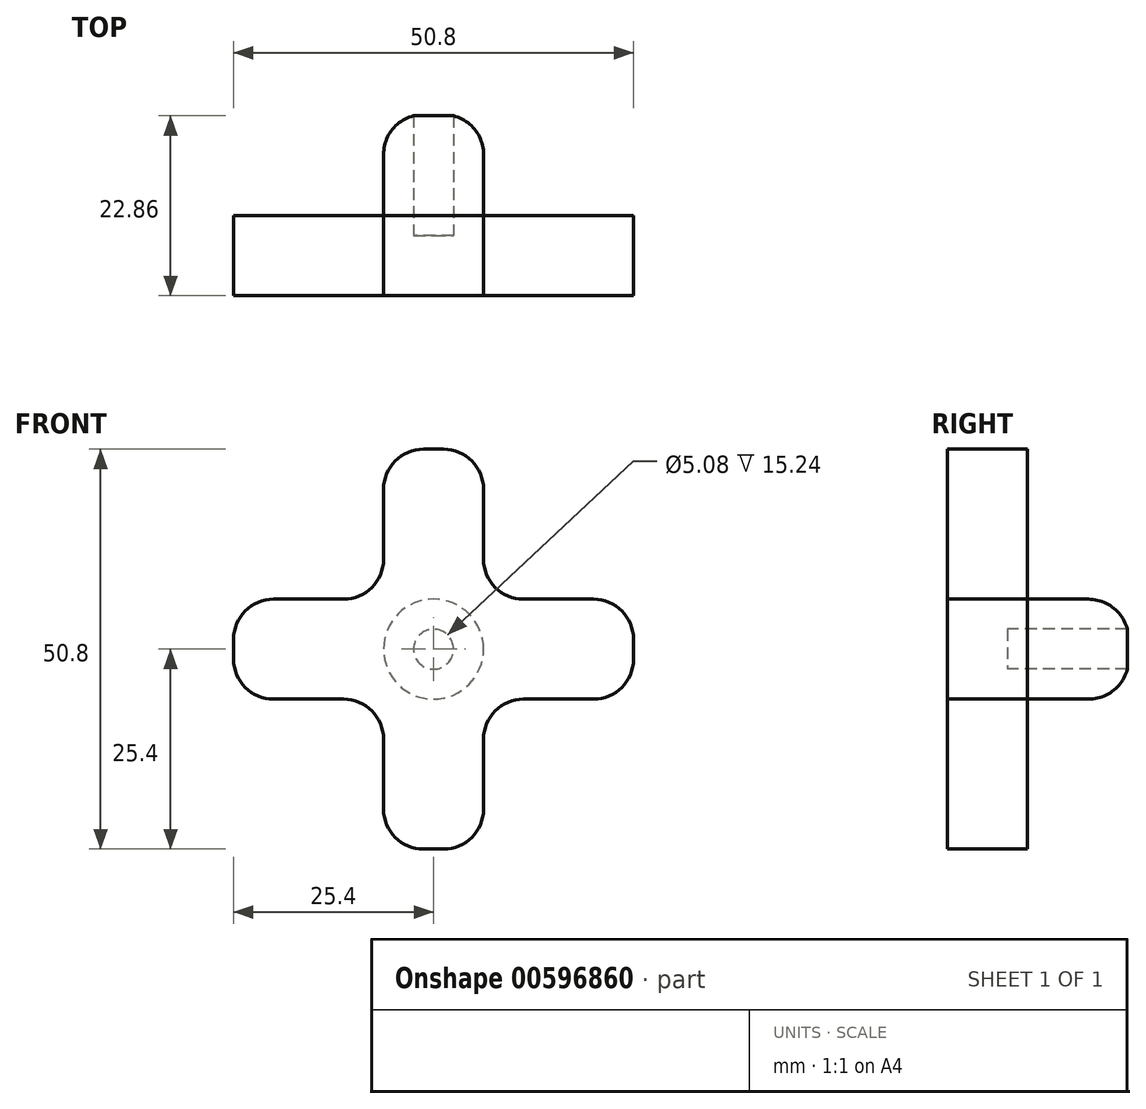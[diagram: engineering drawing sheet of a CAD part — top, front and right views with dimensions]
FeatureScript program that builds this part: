
annotation { "Feature Type Name" : "Feature", "Feature Type Description" : "" }
export const myFeature = defineFeature(function(context is Context, id is Id, definition is map)
    precondition{}
    {
        {
            var Q0;
            Q0=qCreatedBy(makeId("Front.planeOp"),FACE);
            var sketch = newSketch(context, id + "F0", { "sketchPlane" : qUnion([Q0])});
            skLineSegment(sketch, "E0.bottom", {"start": v(0, 0) * mm, "end": v(50.8, 0) * mm});
            skLineSegment(sketch, "E0.top", {"start": v(0, -12.7) * mm, "end": v(50.8, -12.7) * mm});
            skLineSegment(sketch, "E0.left", {"start": v(0, 0) * mm, "end": v(0, -12.7) * mm});
            skLineSegment(sketch, "E0.right", {"start": v(50.8, 0) * mm, "end": v(50.8, -12.7) * mm});
            skLineSegment(sketch, "E1.bottom", {"start": v(19.05, 19.05) * mm, "end": v(31.75, 19.05) * mm});
            skLineSegment(sketch, "E1.top", {"start": v(19.05, -31.75) * mm, "end": v(31.75, -31.75) * mm});
            skLineSegment(sketch, "E1.left", {"start": v(19.05, 19.05) * mm, "end": v(19.05, -31.75) * mm});
            skLineSegment(sketch, "E1.right", {"start": v(31.75, 19.05) * mm, "end": v(31.75, -31.75) * mm});
            skPoint(sketch, "E1.middle", {"position": v(25.4, -6.35) * mm});
            skPoint(sketch, "E1.middle.positionSnap0", {"position": v(0, -6.35) * mm});
            skPoint(sketch, "E1.middle.positionSnap1", {"position": v(25.4, -12.7) * mm});
            skPoint(sketch, "E1.centerSnap0", {"position": v(0, -6.35) * mm});
            skPoint(sketch, "E1.centerSnap1", {"position": v(25.4, -12.7) * mm});
            skSolve(sketch);
        }
        {
            var Q0;
            Q0 = qSketchRegion(id + "F0", true);
            extrude(context, id + "F1", {"entities" : qUnion([Q0]), "depth" : 10.16 * mm, "offsetDistance" : 25.4 * mm});
        }
        {
            var Q0;
            Q0=makeQuery(id+"F1.opExtrude","SWEPT_EDGE",EDGE,{"disambiguationData":[OSD([sQuery(id+"F0.wireOp",EDGE,"E0.top"),sQuery(id+"F0.wireOp",EDGE,"E1.left")])]});
            var Q1;
            Q1=makeQuery(id+"F1.opExtrude","SWEPT_EDGE",EDGE,{"disambiguationData":[OSD([sQuery(id+"F0.wireOp",EDGE,"E0.bottom"),sQuery(id+"F0.wireOp",EDGE,"E1.left")])]});
            var Q2;
            Q2=makeQuery(id+"F1.opExtrude","SWEPT_EDGE",EDGE,{"disambiguationData":[OSD([sQuery(id+"F0.wireOp",EDGE,"E0.bottom"),sQuery(id+"F0.wireOp",EDGE,"E1.right")])]});
            var Q3;
            Q3=makeQuery(id+"F1.opExtrude","SWEPT_EDGE",EDGE,{"disambiguationData":[OSD([sQuery(id+"F0.wireOp",EDGE,"E0.top"),sQuery(id+"F0.wireOp",EDGE,"E1.right")])]});
            var Q4;
            Q4=makeQuery(id+"F1.opExtrude","SWEPT_EDGE",EDGE,{"disambiguationData":[OSD([sQuery(id+"F0.wireOp",EDGE,"E0.bottom"),sQuery(id+"F0.wireOp",EDGE,"E0.left")])]});
            var Q5;
            Q5=makeQuery(id+"F1.opExtrude","SWEPT_EDGE",EDGE,{"disambiguationData":[OSD([sQuery(id+"F0.wireOp",EDGE,"E0.top"),sQuery(id+"F0.wireOp",EDGE,"E0.left")])]});
            var Q6;
            Q6=makeQuery(id+"F1.opExtrude","SWEPT_EDGE",EDGE,{"disambiguationData":[OSD([sQuery(id+"F0.wireOp",EDGE,"E1.top"),sQuery(id+"F0.wireOp",EDGE,"E1.left")])]});
            var Q7;
            Q7=makeQuery(id+"F1.opExtrude","SWEPT_EDGE",EDGE,{"disambiguationData":[OSD([sQuery(id+"F0.wireOp",EDGE,"E1.top"),sQuery(id+"F0.wireOp",EDGE,"E1.right")])]});
            var Q8;
            Q8=makeQuery(id+"F1.opExtrude","SWEPT_EDGE",EDGE,{"disambiguationData":[OSD([sQuery(id+"F0.wireOp",EDGE,"E0.top"),sQuery(id+"F0.wireOp",EDGE,"E0.right")])]});
            var Q9;
            Q9=makeQuery(id+"F1.opExtrude","SWEPT_EDGE",EDGE,{"disambiguationData":[OSD([sQuery(id+"F0.wireOp",EDGE,"E0.bottom"),sQuery(id+"F0.wireOp",EDGE,"E0.right")])]});
            var Q10;
            Q10=makeQuery(id+"F1.opExtrude","SWEPT_EDGE",EDGE,{"disambiguationData":[OSD([sQuery(id+"F0.wireOp",EDGE,"E1.bottom"),sQuery(id+"F0.wireOp",EDGE,"E1.right")])]});
            var Q11;
            Q11=makeQuery(id+"F1.opExtrude","SWEPT_EDGE",EDGE,{"disambiguationData":[OSD([sQuery(id+"F0.wireOp",EDGE,"E1.bottom"),sQuery(id+"F0.wireOp",EDGE,"E1.left")])]});
            fillet(context, id + "F2", {"entities" : qUnion([Q0, Q1, Q2, Q3, Q4, Q5, Q6, Q7, Q8, Q9, Q10, Q11]), "radius" : 5.08 * mm, "tangentPropagation" : true, "allowEdgeOverflow" : false});
        }
        {
            var Q0;
            Q0=makeQuery(id+"F1.opExtrude","CAP_FACE",FACE,{"disambiguationData":[OSD([sQuery(id+"F0.wireOp",EDGE,"E0.bottom"),sQuery(id+"F0.wireOp",EDGE,"E0.top"),sQuery(id+"F0.wireOp",EDGE,"E0.left"),sQuery(id+"F0.wireOp",EDGE,"E0.right"),sQuery(id+"F0.wireOp",EDGE,"E1.bottom"),sQuery(id+"F0.wireOp",EDGE,"E1.top"),sQuery(id+"F0.wireOp",EDGE,"E1.left"),sQuery(id+"F0.wireOp",EDGE,"E1.right")])],"isStart":true});
            var sketch = newSketch(context, id + "F3", { "sketchPlane" : qUnion([Q0])});
            skCircle(sketch, "E2", {"center": v(-25.4, -6.35) * mm, "radius": 6.35 * mm});
            skPoint(sketch, "E2.centerSnap0", {"position": v(-50.8, -6.35) * mm});
            skPoint(sketch, "E2.centerSnap1", {"position": v(-25.4, 19.05) * mm});
            skCircle(sketch, "E3", {"center": v(-25.4, -6.35) * mm, "radius": 2.54 * mm});
            skSolve(sketch);
        }
        {
            var Q0;
            Q0 = qSketchRegion(id + "F3", true);
            extrude(context, id + "F4", {"entities" : qUnion([Q0]), "operationType" : NewBodyOperationType.ADD, "depth" : 12.7 * mm, "offsetDistance" : 25.4 * mm});
        }
        {
            var Q0;
            Q0=makeQuery(id+"F4.boolean.opBoolean","SPLIT",FACE,{"disambiguationData":[TD([makeQuery(id+"F4.opExtrude","SWEPT_FACE",FACE,{"disambiguationData":[OSD([sQuery(id+"F3.wireOp",EDGE,"E3")])]})])],"derivedFrom":makeQuery(id+"F1.opExtrude","CAP_FACE",FACE,{"disambiguationData":[OSD([sQuery(id+"F0.wireOp",EDGE,"E0.bottom"),sQuery(id+"F0.wireOp",EDGE,"E0.top"),sQuery(id+"F0.wireOp",EDGE,"E0.left"),sQuery(id+"F0.wireOp",EDGE,"E0.right"),sQuery(id+"F0.wireOp",EDGE,"E1.bottom"),sQuery(id+"F0.wireOp",EDGE,"E1.top"),sQuery(id+"F0.wireOp",EDGE,"E1.left"),sQuery(id+"F0.wireOp",EDGE,"E1.right")])],"isStart":true})});
            extrude(context, id + "F5", {"entities" : qUnion([Q0]), "operationType" : NewBodyOperationType.REMOVE, "oppositeDirection" : true, "depth" : 2.54 * mm, "offsetDistance" : 25.4 * mm});
        }
        {
            var Q0;
            Q0=makeQuery(id+"F4.opExtrude","CAP_EDGE",EDGE,{"disambiguationData":[OSD([sQuery(id+"F3.wireOp",EDGE,"E2")])],"isStart":false});
            fillet(context, id + "F6", {"entities" : qUnion([Q0]), "radius" : 5.08 * mm, "tangentPropagation" : true, "allowEdgeOverflow" : false});
        }
    });
